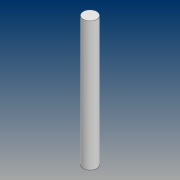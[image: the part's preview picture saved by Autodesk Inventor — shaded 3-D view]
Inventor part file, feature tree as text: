
AUTODESK INVENTOR PART (.ipt)
format: ipt  version: 2021 (Build 250183000, 183)  size: 73,216 bytes
history: native  units: mm
features: extrude x1, sketch x1
ambient origin geometry x8: Origin, YZ Plane, XZ Plane, XY Plane, X Axis, Y Axis, Z Axis, Center Point
bodies: Solid1 (feature_tree)
feature tree (2):
  extrude  "Extrusion1"  Depth=95.0mm TaperAngle=0.0deg
  sketch  "Sketch1"  dims[d0=10.0mm d1=95.0mm d2=0.0mm]
